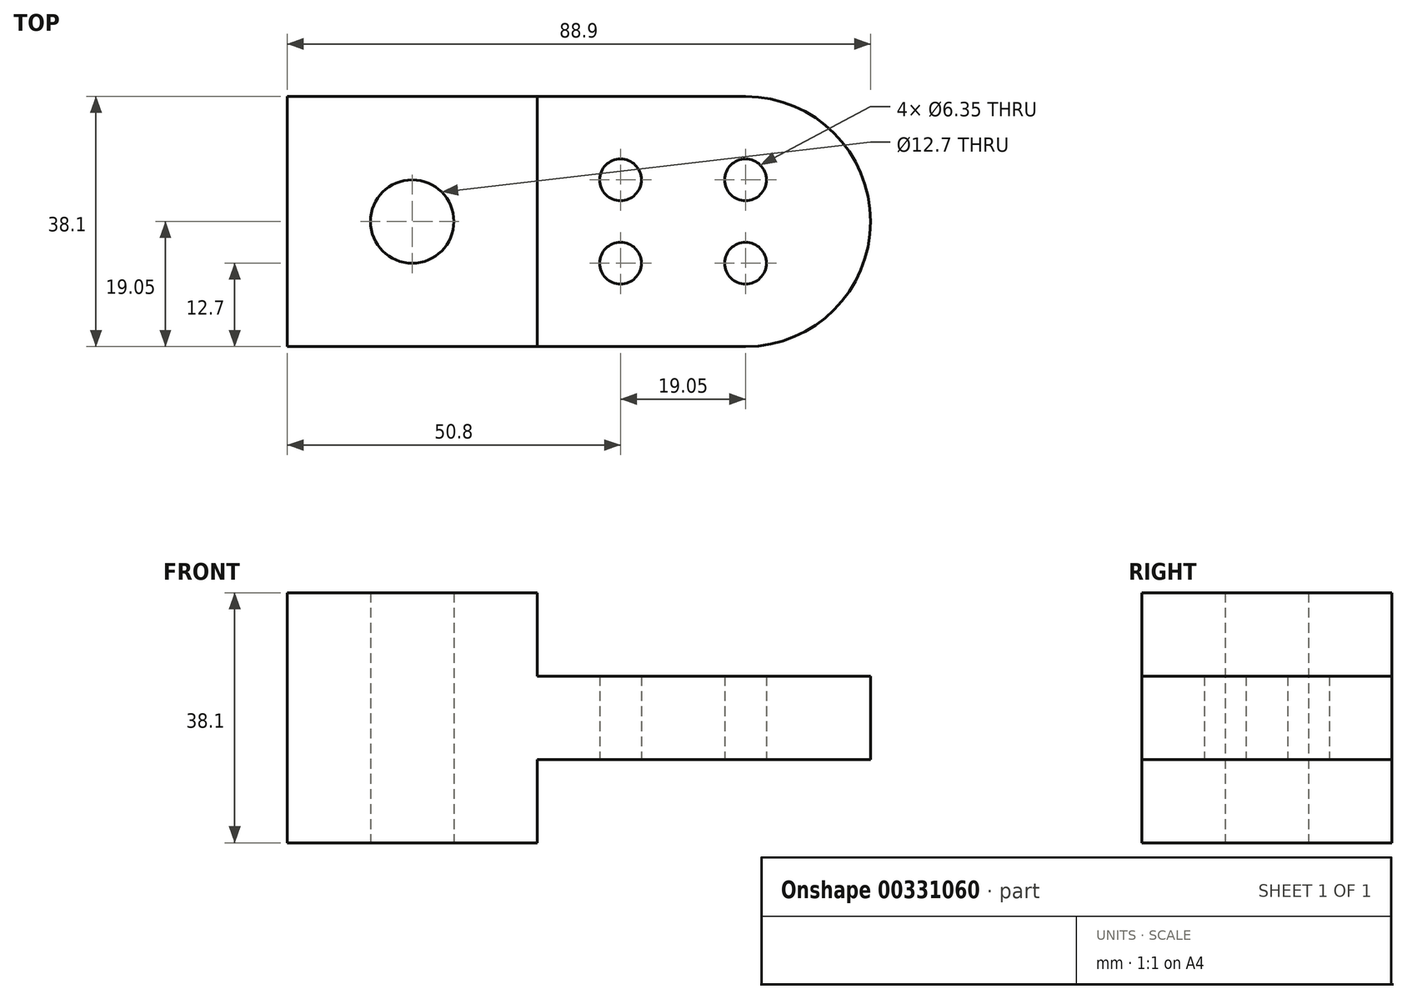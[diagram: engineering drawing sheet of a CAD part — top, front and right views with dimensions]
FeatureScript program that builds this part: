
annotation { "Feature Type Name" : "Feature", "Feature Type Description" : "" }
export const myFeature = defineFeature(function(context is Context, id is Id, definition is map)
    precondition{}
    {
        {
            var Q0;
            Q0=qCreatedBy(makeId("Top.planeOp"),FACE);
            var sketch = newSketch(context, id + "F0", { "sketchPlane" : qUnion([Q0])});
            skLineSegment(sketch, "E0.bottom", {"start": v(0, 0) * mm, "end": v(38.1, 0) * mm});
            skLineSegment(sketch, "E0.top", {"start": v(0, 38.1) * mm, "end": v(38.1, 38.1) * mm});
            skLineSegment(sketch, "E0.left", {"start": v(0, 0) * mm, "end": v(0, 38.1) * mm});
            skLineSegment(sketch, "E0.right", {"start": v(38.1, 0) * mm, "end": v(38.1, 38.1) * mm});
            skLineSegment(sketch, "E1.bottom", {"start": v(38.1, 38.1) * mm, "end": v(69.85, 38.1) * mm});
            skLineSegment(sketch, "E1.top", {"start": v(38.1, 0) * mm, "end": v(69.85, 0) * mm});
            skLineSegment(sketch, "E1.left", {"start": v(38.1, 38.1) * mm, "end": v(38.1, 0) * mm});
            skArc(sketch, "E2", {"start": v(69.85, 0) * mm, "mid": v(88.9, 19.05) * mm, "end": v(69.85, 38.1) * mm});
            skCircle(sketch, "E3", {"center": v(50.8, 12.7) * mm, "radius": 3.18 * mm});
            skCircle(sketch, "E4", {"center": v(50.8, 25.4) * mm, "radius": 3.18 * mm});
            skCircle(sketch, "E5", {"center": v(69.85, 25.4) * mm, "radius": 3.18 * mm});
            skCircle(sketch, "E6", {"center": v(69.85, 12.7) * mm, "radius": 3.18 * mm});
            skCircle(sketch, "E7", {"center": v(19.05, 19.05) * mm, "radius": 6.35 * mm});
            skSolve(sketch);
        }
        {
            var Q0;
            Q0=makeQuery(id+"F0.imprint","IMPRINT",FACE,{"disambiguationData":[TD([[makeQuery(id+"F0.imprint","IMPRINT",EDGE,{"derivedFrom":sQuery(id+"F0.wireOp",EDGE,"E0.bottom")}),1.0]])]});
            extrude(context, id + "F1", {"entities" : qUnion([Q0]), "endBound" : BoundingType.SYMMETRIC, "depth" : 38.1 * mm});
        }
        {
            var Q0;
            Q0=makeQuery(id+"F0.imprint","IMPRINT",FACE,{"disambiguationData":[TD([[makeQuery(id+"F0.imprint","IMPRINT",EDGE,{"derivedFrom":sQuery(id+"F0.wireOp",EDGE,"E1.bottom")}),-1.0]])]});
            extrude(context, id + "F2", {"entities" : qUnion([Q0]), "operationType" : NewBodyOperationType.ADD, "endBound" : BoundingType.SYMMETRIC, "depth" : 12.7 * mm});
        }
    });
